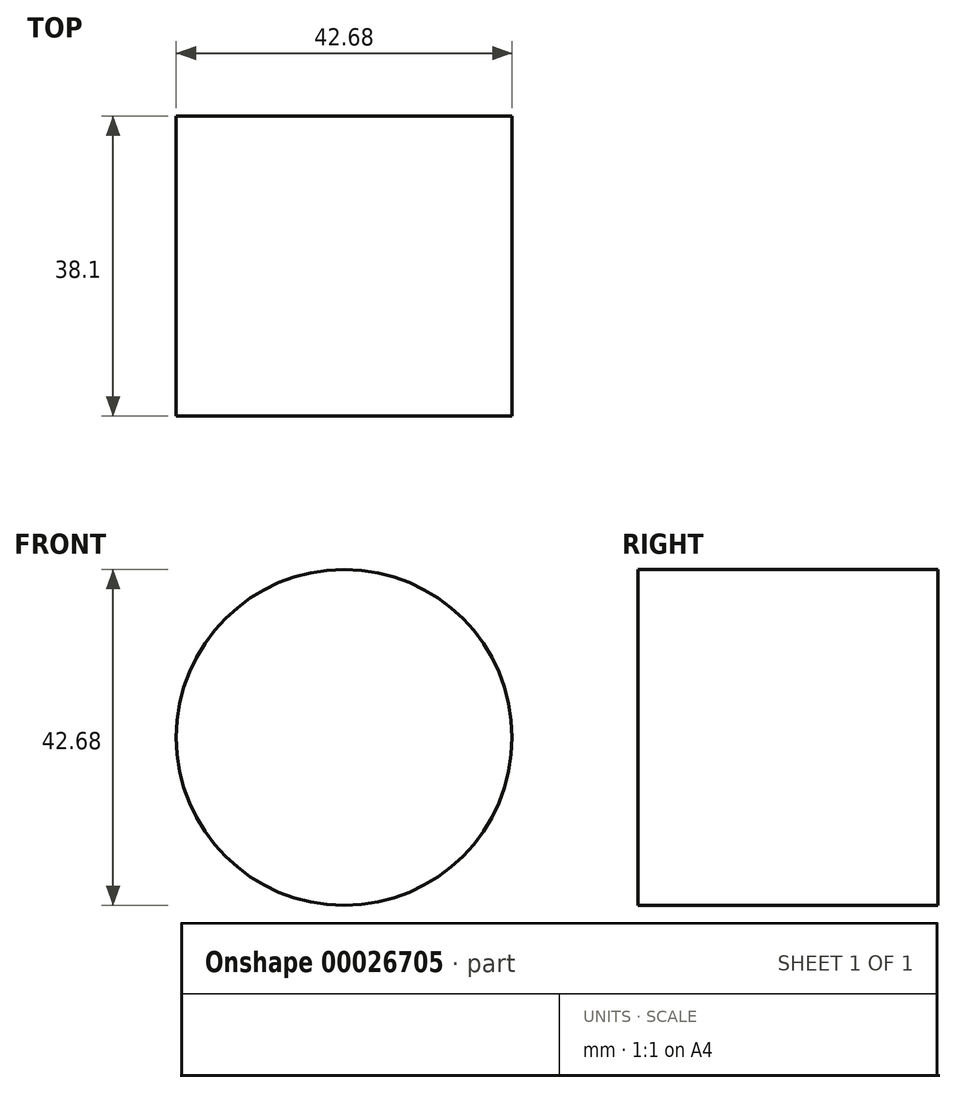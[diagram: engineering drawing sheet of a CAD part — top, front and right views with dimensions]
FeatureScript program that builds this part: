
annotation { "Feature Type Name" : "Feature", "Feature Type Description" : "" }
export const myFeature = defineFeature(function(context is Context, id is Id, definition is map)
    precondition{}
    {
        {
            var Q0;
            Q0=qCreatedBy(makeId("Front.planeOp"),FACE);
            var sketch = newSketch(context, id + "F0", { "sketchPlane" : qUnion([Q0])});
            skCircle(sketch, "E0", {"center": v(0, 0) * mm, "radius": 21.34 * mm});
            skSolve(sketch);
        }
        {
            var Q0;
            Q0 = qSketchRegion(id + "F0", true);
            extrude(context, id + "F1", {"entities" : qUnion([Q0]), "depth" : 38.1 * mm});
        }
    });
